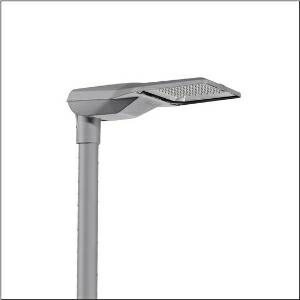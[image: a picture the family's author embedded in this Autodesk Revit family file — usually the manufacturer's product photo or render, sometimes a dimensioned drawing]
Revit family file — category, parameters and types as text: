
# Revit family: streetlight_sl_21_iq_midi___st1_0a_5xe3d31g08mb_3419
name_source: partatom
category: Lighting Fixtures
units: mm (PartAtom-declared; Revit-internal decimal feet)

## family parameters
Cut with Voids When Loaded = No
Host = Face
Light Source = No
Part Type = Normal
Room Calculation Point = No
Round Connector Dimension = Use Diameter
Shared = No

## types (1)
- --- (1 x LED, 19500 lm, 146.7 W, 3000K)
    Apparent Load = 147 VA
    CIE Flux Codes = 37 72 97 100 100
    Color Rendering = 70
    Color Temperature = 3000K
    Default Elevation = 1800 mm
    Description = Streetlight SL 21 iQ midi, mast luminaire, primary light control with lens, of PMMA, primary optical cover: cover, of toughened safety glass, transparent, light distribution: ST1.0a, light emission: direct distribution, primary light characteristic: asymmetric, installation type: post-top, side-entry, LED, High Power LED, rated luminous flux: 19.500lm, luminous efficacy: 133lm/W, light colour: 730, colour temperature: 3000K, control gear: iQ Street-Remote, control: Street-Remote, Auto-Match, Temp-Guard, Lumen-Switch, Night-Set, Smart-Wire, Light-Fading, Desk-Remote (wireless, voltage-free reading and setting of iQ features in the workshop via application-optimized NFC function/RFID function), optimised constant luminous flux control (CLO 2.0), pre-setting: linear dimming characteristic, mains connection: 230..240V, AC, 50/60Hz, start of lifetime: 147W, end of service life: 161W, reduction: 62W, luminaire housing, of diecast aluminium, powder-coated, SITECO metallic grey (DB 702S), corrosivity category C5 high according to DIN EN ISO 12944, please order mast flange separately, inclination adjustable: 0°, 5°, 10°, 15°, sealing non-destructively replaceable, multi-level sealing system, length: 644mm, width: 335mm, height: 110mm, mast flange for spigot size: 42mm (side-entry): 5XC10008XM4, 60/48mm (side-entry/post-top): 5XC10108XM2, 76/60mm (side-entry/post-top): 5XC10108XM1, mounting height: 4..8m, protection rating (complete): IP66, insulation class (complete): insulation class II (safety insulation), certification: CE, ENEC, ENEC+, VDE, impact resistance: IK10, permissible operating ambient temperature for outdoor applications: -40..+50°C, standard-compliant lighting for roads and squares, packaging unit: 1 piece

Light Distribution: ST1.0a
    Height = 111 mm
    Lamp = 1 x LED
    Lamp Light Flux = 19500 lm
    Lamp Power = 146.7 W
    Lamp count = 1
    Length = 644 mm
    Luminous efficacy = 133 lm/W
    Manufacturer = Siteco
    ModVariant = No
    Model = 5XE3D31G08MB
    Number of Poles = 1
    OnlyDefault = Yes
    Power Factor = 1
    Product Name = Streetlight SL 21 iQ midi | ST1.0a
    Product group = mast luminaire | pylon top
    ProductGroupID = 6100
    Protection Class = Protection class II
    Protection Degree = IP 66
    RLX_Detail_Level = 1
    RLX_Emergency_Light_Flux = 0 lm
    RLX_Emergency_Type = 0
    RLX_Emergency_Type_DB = No
    RlxData = <blob elided: 26929 chars, md5=7ebf781a>
    Socket = socket
    Standby Power = 0 W
    System Light Flux = 19499 lm
    System Power = 147 W
    Type Comments = factory setting: luminous flux: 100 % | dim-lin: 254 | 753 mA
    Type Image = l_1004298.jpg
    URL = http://relux.com
    VarID = @adj_186959
    Voltage = 0 V
    Weight = 0.00 kg
    Width = 336 mm

## geometry (parser evidence)
native form markers: Blend x4, Sweep x13
no freeform markers — native parametric forms only
